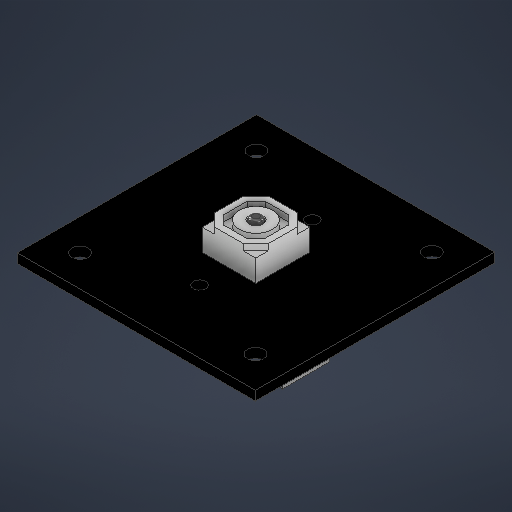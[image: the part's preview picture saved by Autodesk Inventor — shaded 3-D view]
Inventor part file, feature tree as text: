
AUTODESK INVENTOR PART (.ipt)
format: ipt  version: 2025.1 (Build 291241000, 241)  size: 299,008 bytes
history: native  units: mm
features: extrude x6, sketch x2, fillet x1
ambient origin geometry x8: Origin, YZ Plane, XZ Plane, XY Plane, X Axis, Y Axis, Z Axis, Center Point
bodies: Solid1 (feature_tree)
feature tree (9):
  sketch  "Sketch1"  dims[d0=38.0mm d1=38.2mm]
  extrude  "Extrusion1"  Depth=38.2mm
  extrude  "Extrusion2"  Depth=2.0mm
  extrude  "Extrusion3"  Depth=2.0mm
  extrude  "Extrusion4"  Depth=9.0mm
  extrude  "Extrusion5"  Depth=9.0mm
  extrude  "Extrusion6"  Depth=2.6mm
  fillet  "Fillet1"  Radius=2.6mm
  sketch  "Sketch2"  dims[d2=8.55mm d3=2.0mm d4=2.0mm d5=9.0mm d6=9.0mm d7=2.6mm d8=2.6mm d9=2.6mm d10=2.6mm d11=28.0mm d12=1.5mm d13=0.0mm d14=4.5mm d15=0.0mm d16=8.32mm d17=7.5mm d18=3.5mm d19=4.0mm d20=4.5mm d21=0.0mm d23=0.4mm d24=45.0deg d25=2.0mm d26=5.3mm d27=2.3mm d28=1.0mm d29=0.0mm d30=1.0mm d31=1.0mm d32=1.0mm d33=1.0mm d34=1.0mm d35=1.0mm d36=1.0mm d37=1.0mm d38=1.0mm d39=0.0mm d40=2.0mm d41=1.5mm d42=0.0mm d43=0.5mm]
